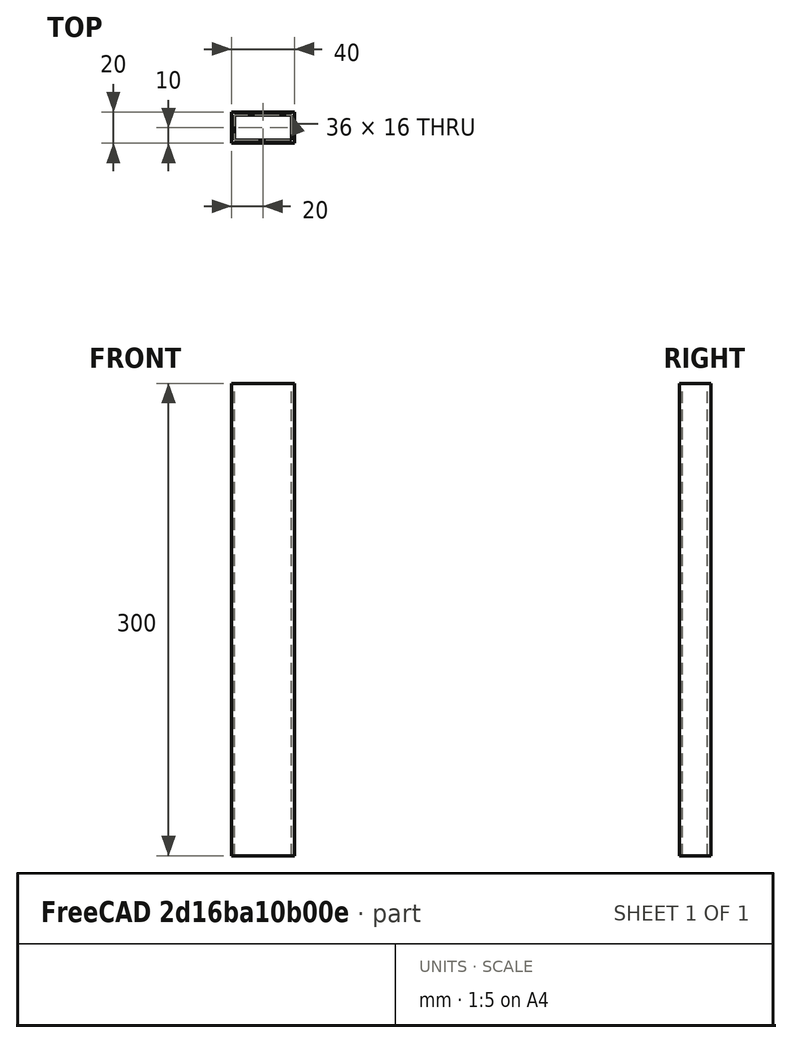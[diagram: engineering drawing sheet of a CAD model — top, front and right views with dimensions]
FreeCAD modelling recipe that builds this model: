
FCSTD DOCUMENT  (FreeCAD 0.20R29177 (Git))
Label: Tube
License: All rights reserved
LicenseURL: http://en.wikipedia.org/wiki/All_rights_reserved
objects: Sketcher::SketchObject×3, PartDesign::Body×2, PartDesign::Pad×1
note: 7 computed .brp shape members not serialized (recipe doc carries the construction recipe); baked Part::Feature solids carry a one-line shape summary decoded from their .brp

FEATURE [Sketcher::SketchObject] Sketch
  FullyConstrained = true
  MapMode = 5
  Support = -> [XY_Plane]
  sketch-geometry (8):
    g0: LineSegment StartX=-20 StartY=-10 StartZ=0 EndX=20 EndY=-10 EndZ=0
    g1: LineSegment StartX=20 StartY=-10 StartZ=0 EndX=20 EndY=10 EndZ=0
    g2: LineSegment StartX=20 StartY=10 StartZ=0 EndX=-20 EndY=10 EndZ=0
    g3: LineSegment StartX=-20 StartY=10 StartZ=0 EndX=-20 EndY=-10 EndZ=0
    g4: LineSegment StartX=-18 StartY=8 StartZ=0 EndX=18 EndY=8 EndZ=0
    g5: LineSegment StartX=18 StartY=8 StartZ=0 EndX=18 EndY=-8 EndZ=0
    g6: LineSegment StartX=18 StartY=-8 StartZ=0 EndX=-18 EndY=-8 EndZ=0
    g7: LineSegment StartX=-18 StartY=-8 StartZ=0 EndX=-18 EndY=8 EndZ=0
  constraints (24):
    c: Coincident(g0,g1)
    c: Coincident(g1,g2)
    c: Coincident(g2,g3)
    c: Coincident(g3,g0)
    c: Horizontal(g0)
    c: Horizontal(g2)
    c: Vertical(g1)
    c: Vertical(g3)
    c: DistanceX(g2,g2) = 40
    c: Distance(g3) = 20
    c: Distance(g-1,g2) = 10
    c: Distance(g-1,g1) = 20
    c: Coincident(g4,g5)
    c: Coincident(g5,g6)
    c: Coincident(g6,g7)
    c: Coincident(g7,g4)
    c: Horizontal(g4)
    c: Horizontal(g6)
    c: Vertical(g5)
    c: Vertical(g7)
    c: Distance(g4,g2) = 2
    c: Distance(g6,g3) = 2
    c: Distance(g5,g1) = 2
    c: Distance(g5,g0) = 2
FEATURE [PartDesign::Pad] Pad
  Direction = (0,0,1)
  Length = 300
  Length2 = 10
  Midplane = true
  Profile = -> Sketch
  ReferenceAxis = -> Sketch [N_Axis]
  Refine = true
  Type = 0
FEATURE [Sketcher::SketchObject] Sketch001
  ExternalGeometry = -> [Pad]
  FullyConstrained = true
  MapMode = 5
  Placement = pos=(0,-10,0) rot=(1,0,0;1.5708rad)
  Support = -> [Pad]
FEATURE [PartDesign::Body] Body  label="tube"
  Group = -> [Sketch,Pad,Sketch001]
  Origin = -> Origin
  Tip = -> Pad
FEATURE [Sketcher::SketchObject] Sketch002
  FullyConstrained = true
  MapMode = 5
  Support = -> [XY_Plane001]
  sketch-geometry (4):
    g0: LineSegment StartX=-25 StartY=20 StartZ=0 EndX=25 EndY=20 EndZ=0
    g1: LineSegment StartX=25 StartY=20 StartZ=0 EndX=25 EndY=-20 EndZ=0
    g2: LineSegment StartX=25 StartY=-20 StartZ=0 EndX=-25 EndY=-20 EndZ=0
    g3: LineSegment StartX=-25 StartY=-20 StartZ=0 EndX=-25 EndY=20 EndZ=0
  constraints (12):
    c: Coincident(g0,g1)
    c: Coincident(g1,g2)
    c: Coincident(g2,g3)
    c: Coincident(g3,g0)
    c: Horizontal(g0)
    c: Horizontal(g2)
    c: Vertical(g1)
    c: Vertical(g3)
    c: Distance(g0) = 50
    c: Distance(g3) = 40
    c: Distance(g0,g-2) = 25
    c: Distance(g2,g-1) = 20
FEATURE [PartDesign::Body] Body001
  Group = -> [Sketch002]
  Origin = -> Origin001
